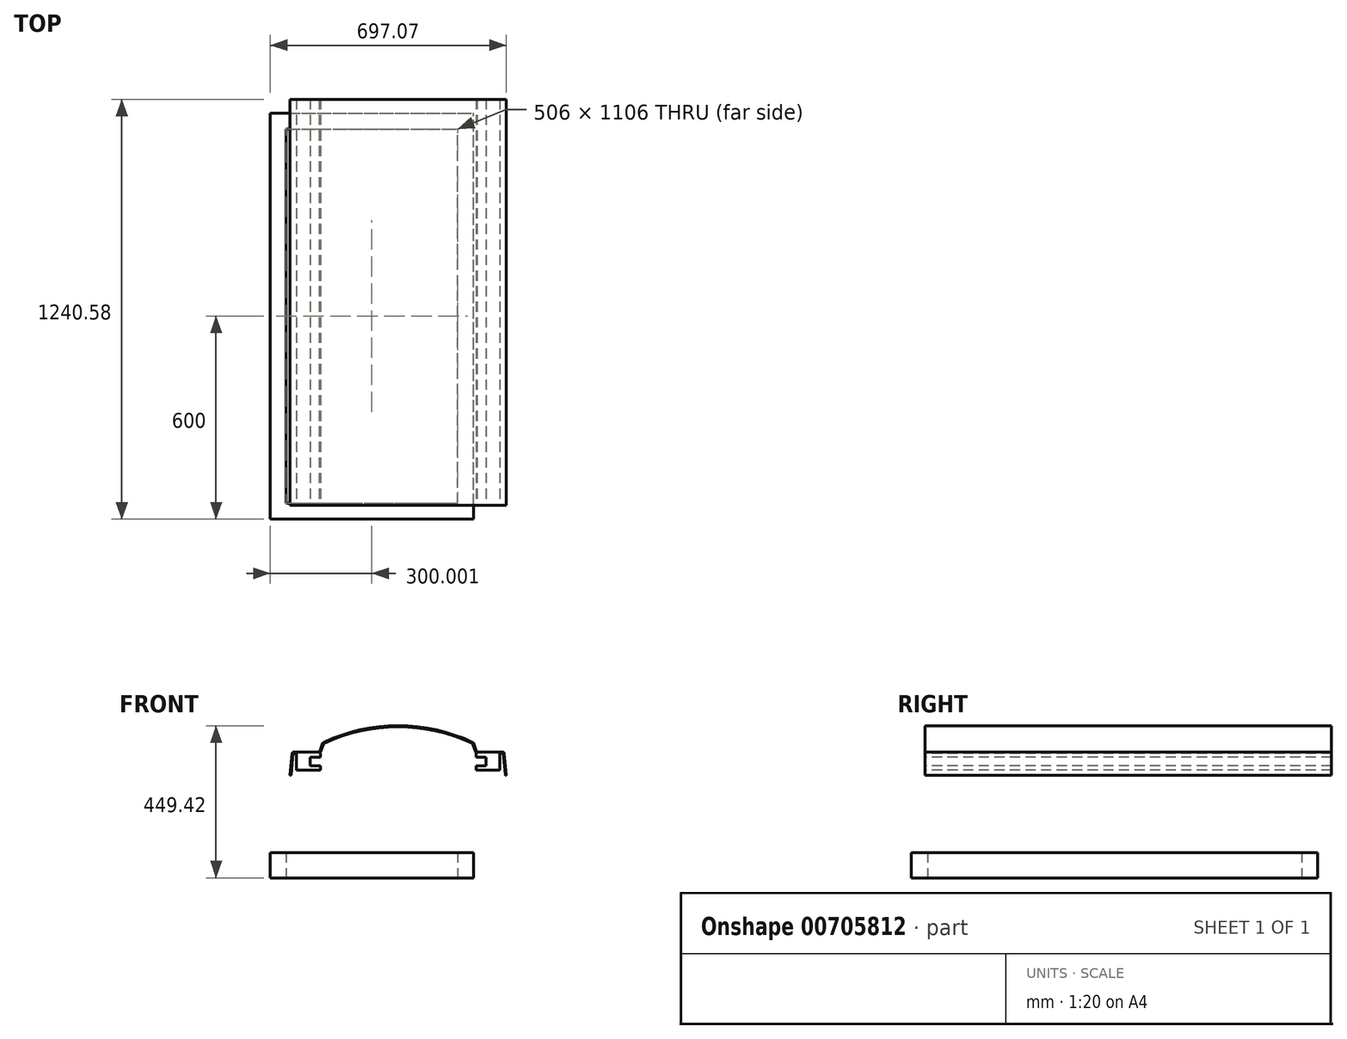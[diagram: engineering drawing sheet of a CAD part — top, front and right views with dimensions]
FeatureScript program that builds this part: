
annotation { "Feature Type Name" : "Feature", "Feature Type Description" : "" }
export const myFeature = defineFeature(function(context is Context, id is Id, definition is map)
    precondition{}
    {
        {
            var Q0;
            Q0=qCreatedBy(makeId("Top.planeOp"),FACE);
            var sketch = newSketch(context, id + "F0", { "sketchPlane" : qUnion([Q0])});
            skLineSegment(sketch, "E0.bottom", {"start": v(-38.49, -40.58) * mm, "end": v(561.51, -40.58) * mm});
            skLineSegment(sketch, "E0.top", {"start": v(-38.49, 1159.42) * mm, "end": v(561.51, 1159.42) * mm});
            skLineSegment(sketch, "E0.left", {"start": v(-38.49, -40.58) * mm, "end": v(-38.49, 1159.42) * mm});
            skLineSegment(sketch, "E0.right", {"start": v(561.51, -40.58) * mm, "end": v(561.51, 1159.42) * mm});
            skLineSegment(sketch, "E1.bottom", {"start": v(8.51, 6.42) * mm, "end": v(514.51, 6.42) * mm});
            skLineSegment(sketch, "E1.top", {"start": v(8.51, 1112.42) * mm, "end": v(514.51, 1112.42) * mm});
            skLineSegment(sketch, "E1.left", {"start": v(8.51, 6.42) * mm, "end": v(8.51, 1112.42) * mm});
            skLineSegment(sketch, "E1.right", {"start": v(514.51, 6.42) * mm, "end": v(514.51, 1112.42) * mm});
            skSolve(sketch);
        }
        {
            var Q0;
            Q0=makeQuery(id+"F0.imprint","IMPRINT",FACE,{"disambiguationData":[TD([[makeQuery(id+"F0.imprint","IMPRINT",EDGE,{"derivedFrom":sQuery(id+"F0.wireOp",EDGE,"E0.bottom")}),1.0]])]});
            extrude(context, id + "F1", {"entities" : qUnion([Q0]), "depth" : 75 * mm, "offsetDistance" : 25 * mm});
        }
        {
            var Q0;
            Q0=qCreatedBy(makeId("Front.planeOp"),FACE);
            var sketch = newSketch(context, id + "F2", { "sketchPlane" : qUnion([Q0])});
            skLineSegment(sketch, "E2", {"start": v(39.17, 318.42) * mm, "end": v(109.17, 318.42) * mm});
            skLineSegment(sketch, "E3", {"start": v(39.17, 318.42) * mm, "end": v(39.17, 368.42) * mm});
            skLineSegment(sketch, "E4", {"start": v(39.17, 368.42) * mm, "end": v(106.35, 368.42) * mm});
            skLineSegment(sketch, "E5", {"start": v(109.17, 368.42) * mm, "end": v(109.17, 355.92) * mm});
            skLineSegment(sketch, "E6", {"start": v(109.17, 330.92) * mm, "end": v(79.17, 330.92) * mm});
            skLineSegment(sketch, "E7", {"start": v(79.17, 330.92) * mm, "end": v(79.17, 355.92) * mm});
            skLineSegment(sketch, "E8", {"start": v(79.17, 355.92) * mm, "end": v(109.17, 355.92) * mm});
            skPoint(sketch, "E9", {"position": v(29.17, 368.42) * mm});
            skPoint(sketch, "E10", {"position": v(24.17, 318.42) * mm});
            skLineSegment(sketch, "E11", {"start": v(29.08, 367.51) * mm, "end": v(22.76, 304.32) * mm});
            skLineSegment(sketch, "E12", {"start": v(30.08, 368.42) * mm, "end": v(39.17, 368.42) * mm});
            skLineSegment(sketch, "E13", {"start": v(21.77, 303.42) * mm, "end": v(20.76, 303.42) * mm});
            skLineSegment(sketch, "E14", {"start": v(106.35, 371.42) * mm, "end": v(30.08, 371.42) * mm});
            skLineSegment(sketch, "E15", {"start": v(26.1, 367.81) * mm, "end": v(19.77, 304.51) * mm});
            skLineSegment(sketch, "E16", {"start": v(119.03, 396.03) * mm, "end": v(110.12, 371.07) * mm});
            skPoint(sketch, "E17.visualSharp", {"position": v(19.66, 303.42) * mm});
            skArc(sketch, "E17.filletArc", {"start": v(19.77, 304.51) * mm, "mid": v(20.02, 303.74) * mm, "end": v(20.76, 303.42) * mm});
            skPoint(sketch, "E18.visualSharp", {"position": v(22.67, 303.42) * mm});
            skArc(sketch, "E18.filletArc", {"start": v(21.77, 303.42) * mm, "mid": v(22.44, 303.67) * mm, "end": v(22.76, 304.32) * mm});
            skArc(sketch, "E19.filletArc", {"start": v(30.08, 368.42) * mm, "mid": v(29.4, 368.16) * mm, "end": v(29.08, 367.51) * mm});
            skPoint(sketch, "E20.visualSharp", {"position": v(26.46, 371.42) * mm});
            skArc(sketch, "E20.filletArc", {"start": v(30.08, 371.42) * mm, "mid": v(27.4, 370.38) * mm, "end": v(26.1, 367.81) * mm});
            skPoint(sketch, "E21.visualSharp", {"position": v(109.17, 368.42) * mm});
            skArc(sketch, "E21.filletArc", {"start": v(106.35, 368.42) * mm, "mid": v(108.66, 369.15) * mm, "end": v(110.12, 371.07) * mm});
            skLineSegment(sketch, "E22", {"start": v(109.17, 368.42) * mm, "end": v(106.35, 368.42) * mm});
            skLineSegment(sketch, "E23.trimOffspring", {"start": v(109.17, 330.92) * mm, "end": v(109.17, 318.42) * mm});
            skLineSegment(sketch, "E24", {"start": v(116.5, 397.85) * mm, "end": v(107.3, 372.08) * mm});
            skArc(sketch, "E25.filletArc", {"start": v(106.35, 371.42) * mm, "mid": v(106.93, 371.6) * mm, "end": v(107.3, 372.08) * mm});
            skLineSegment(sketch, "E26", {"start": v(339.17, 449.42) * mm, "end": v(339.17, 446.42) * mm});
            skPoint(sketch, "E27.visualSharp", {"position": v(119.17, 396.42) * mm});
            skPoint(sketch, "E28.visualSharp", {"position": v(117.06, 399.42) * mm});
            skArc(sketch, "E29", {"start": v(339.17, 449.42) * mm, "mid": v(226.15, 436.94) * mm, "end": v(118.56, 400.13) * mm});
            skArc(sketch, "E30", {"start": v(339.17, 446.42) * mm, "mid": v(226.57, 433.8) * mm, "end": v(119.54, 396.6) * mm});
            skArc(sketch, "E31.filletArc", {"start": v(119.54, 396.6) * mm, "mid": v(119.23, 396.36) * mm, "end": v(119.03, 396.03) * mm});
            skArc(sketch, "E32.filletArc", {"start": v(118.56, 400.13) * mm, "mid": v(117.3, 399.2) * mm, "end": v(116.5, 397.85) * mm});
            skLineSegment(sketch, "E33.MirrorCS", {"start": v(656.58, 303.42) * mm, "end": v(657.58, 303.42) * mm});
            skArc(sketch, "E34.MirrorCS", {"start": v(656.58, 303.42) * mm, "mid": v(655.9, 303.67) * mm, "end": v(655.58, 304.32) * mm});
            skArc(sketch, "E35.MirrorCS", {"start": v(658.58, 304.51) * mm, "mid": v(658.32, 303.74) * mm, "end": v(657.58, 303.42) * mm});
            skArc(sketch, "E36.MirrorCS", {"start": v(559.78, 400.13) * mm, "mid": v(561.04, 399.2) * mm, "end": v(561.84, 397.85) * mm});
            skArc(sketch, "E37.MirrorCS", {"start": v(558.8, 396.6) * mm, "mid": v(559.11, 396.36) * mm, "end": v(559.3, 396.03) * mm});
            skArc(sketch, "E38.MirrorCS", {"start": v(648.27, 368.42) * mm, "mid": v(648.94, 368.16) * mm, "end": v(649.26, 367.51) * mm});
            skArc(sketch, "E39.MirrorCS", {"start": v(648.27, 371.42) * mm, "mid": v(650.95, 370.38) * mm, "end": v(652.25, 367.81) * mm});
            skLineSegment(sketch, "E40.MirrorCS", {"start": v(569.17, 368.42) * mm, "end": v(572, 368.42) * mm});
            skArc(sketch, "E41.MirrorCS", {"start": v(572, 371.42) * mm, "mid": v(571.41, 371.6) * mm, "end": v(571.05, 372.08) * mm});
            skArc(sketch, "E42.MirrorCS", {"start": v(572, 368.42) * mm, "mid": v(569.69, 369.15) * mm, "end": v(568.22, 371.07) * mm});
            skLineSegment(sketch, "E43.MirrorCS", {"start": v(648.27, 368.42) * mm, "end": v(639.17, 368.42) * mm});
            skLineSegment(sketch, "E44.MirrorCS", {"start": v(569.17, 330.92) * mm, "end": v(569.17, 318.42) * mm});
            skLineSegment(sketch, "E45.MirrorCS", {"start": v(569.17, 368.42) * mm, "end": v(569.17, 355.92) * mm});
            skLineSegment(sketch, "E46.MirrorCS", {"start": v(561.84, 397.85) * mm, "end": v(571.05, 372.08) * mm});
            skPoint(sketch, "E47.MirrorP", {"position": v(561.29, 399.42) * mm});
            skLineSegment(sketch, "E48.MirrorCS", {"start": v(559.3, 396.03) * mm, "end": v(568.22, 371.07) * mm});
            skPoint(sketch, "E49.MirrorP", {"position": v(559.17, 396.42) * mm});
            skPoint(sketch, "E50.MirrorP", {"position": v(649.17, 368.42) * mm});
            skPoint(sketch, "E51.MirrorP", {"position": v(655.67, 303.42) * mm});
            skLineSegment(sketch, "E52.MirrorCS", {"start": v(652.25, 367.81) * mm, "end": v(658.58, 304.51) * mm});
            skLineSegment(sketch, "E53.MirrorCS", {"start": v(572, 371.42) * mm, "end": v(648.27, 371.42) * mm});
            skLineSegment(sketch, "E54.MirrorCS", {"start": v(649.26, 367.51) * mm, "end": v(655.58, 304.32) * mm});
            skLineSegment(sketch, "E55.MirrorCS", {"start": v(599.17, 355.92) * mm, "end": v(569.17, 355.92) * mm});
            skLineSegment(sketch, "E56.MirrorCS", {"start": v(599.17, 330.92) * mm, "end": v(599.17, 355.92) * mm});
            skLineSegment(sketch, "E57.MirrorCS", {"start": v(569.17, 330.92) * mm, "end": v(599.17, 330.92) * mm});
            skLineSegment(sketch, "E58.MirrorCS", {"start": v(639.17, 368.42) * mm, "end": v(572, 368.42) * mm});
            skLineSegment(sketch, "E59.MirrorCS", {"start": v(639.17, 318.42) * mm, "end": v(639.17, 368.42) * mm});
            skLineSegment(sketch, "E60.MirrorCS", {"start": v(639.17, 318.42) * mm, "end": v(569.17, 318.42) * mm});
            skArc(sketch, "E61.MirrorCS", {"start": v(339.17, 449.42) * mm, "mid": v(452.2, 436.94) * mm, "end": v(559.78, 400.13) * mm});
            skPoint(sketch, "E62.MirrorP", {"position": v(569.17, 368.42) * mm});
            skPoint(sketch, "E63.MirrorP", {"position": v(654.17, 318.42) * mm});
            skPoint(sketch, "E64.MirrorP", {"position": v(651.89, 371.42) * mm});
            skPoint(sketch, "E65.MirrorP", {"position": v(658.69, 303.42) * mm});
            skArc(sketch, "E66.MirrorCS", {"start": v(339.17, 446.42) * mm, "mid": v(451.78, 433.8) * mm, "end": v(558.8, 396.6) * mm});
            skSolve(sketch);
        }
        {
            var Q0;
            Q0=makeQuery(id+"F2.imprint","IMPRINT",FACE,{"disambiguationData":[TD([[makeQuery(id+"F2.imprint","IMPRINT",EDGE,{"derivedFrom":sQuery(id+"F2.wireOp",EDGE,"E2")}),1.0]])]});
            var Q1;
            Q1=makeQuery(id+"F2.imprint","IMPRINT",FACE,{"disambiguationData":[TD([[makeQuery(id+"F2.imprint","IMPRINT",EDGE,{"derivedFrom":sQuery(id+"F2.wireOp",EDGE,"E40.MirrorCS")}),-1.0]])]});
            var Q2;
            Q2=makeQuery(id+"F2.imprint","IMPRINT",FACE,{"disambiguationData":[TD([[makeQuery(id+"F2.imprint","IMPRINT",EDGE,{"derivedFrom":sQuery(id+"F2.wireOp",EDGE,"E26")}),1.0]])]});
            var Q3;
            Q3=makeQuery(id+"F2.imprint","IMPRINT",FACE,{"disambiguationData":[TD([[makeQuery(id+"F2.imprint","IMPRINT",EDGE,{"derivedFrom":sQuery(id+"F2.wireOp",EDGE,"E4")}),1.0]])]});
            extrude(context, id + "F3", {"entities" : qUnion([Q0, Q1, Q2, Q3]), "oppositeDirection" : true, "depth" : 1200 * mm, "offsetDistance" : 25 * mm});
        }
    });
